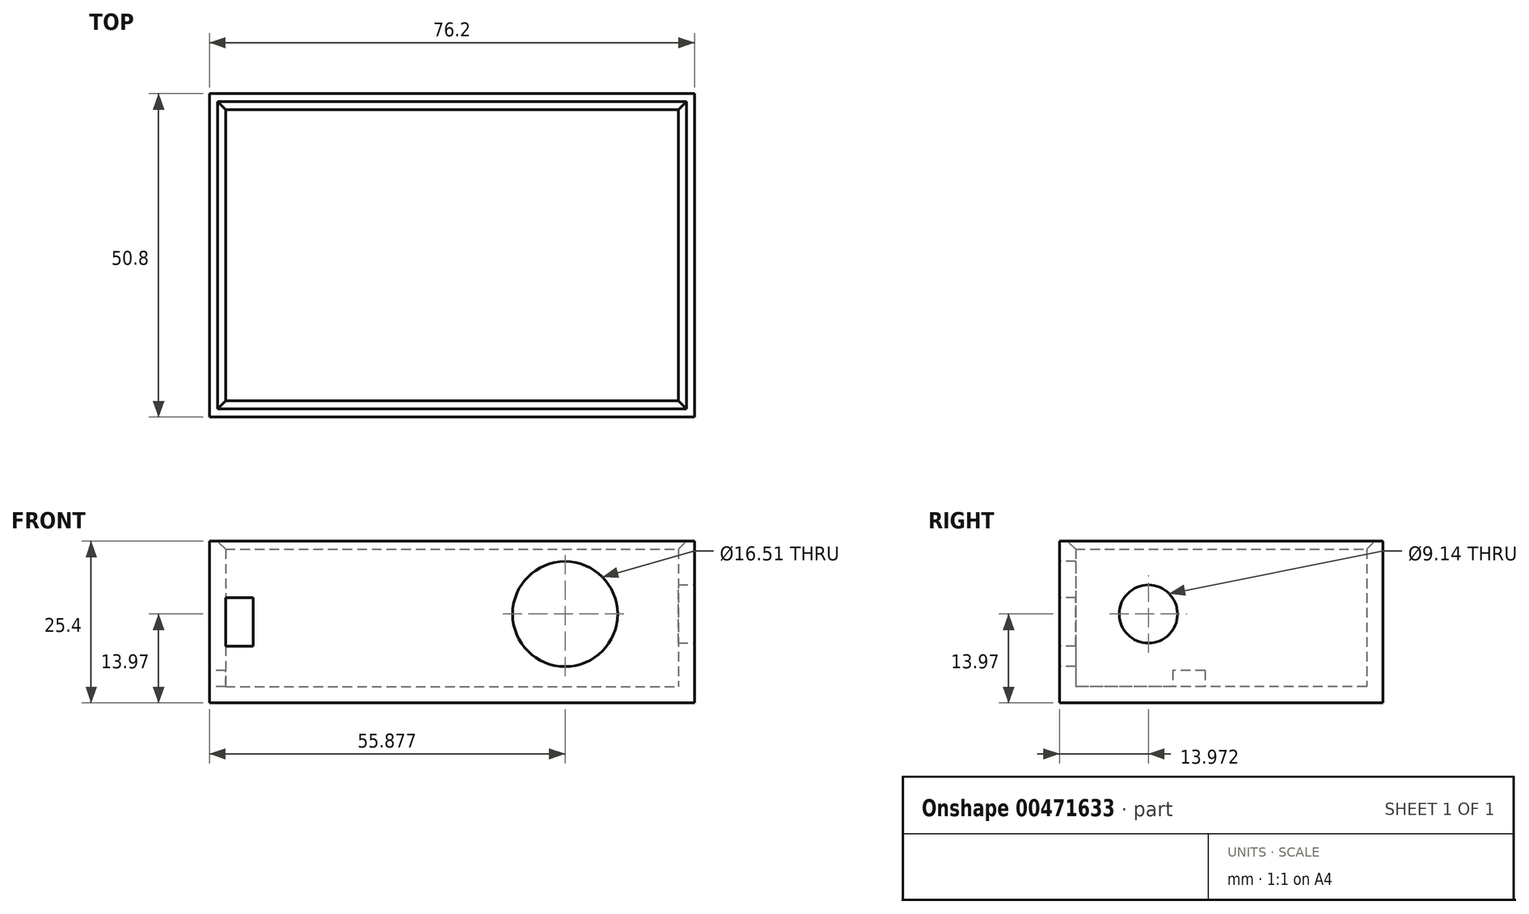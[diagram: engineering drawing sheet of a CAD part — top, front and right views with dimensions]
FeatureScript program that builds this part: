
annotation { "Feature Type Name" : "Feature", "Feature Type Description" : "" }
export const myFeature = defineFeature(function(context is Context, id is Id, definition is map)
    precondition{}
    {
        {
            var Q0;
            Q0=qCreatedBy(makeId("Top.planeOp"),FACE);
            var sketch = newSketch(context, id + "F0", { "sketchPlane" : qUnion([Q0])});
            skLineSegment(sketch, "E0.bottom", {"start": v(-32.94, 25.54) * mm, "end": v(43.26, 25.54) * mm});
            skLineSegment(sketch, "E0.top", {"start": v(-32.94, -25.26) * mm, "end": v(43.26, -25.26) * mm});
            skLineSegment(sketch, "E0.left", {"start": v(-32.94, 25.54) * mm, "end": v(-32.94, -25.26) * mm});
            skLineSegment(sketch, "E0.right", {"start": v(43.26, 25.54) * mm, "end": v(43.26, -25.26) * mm});
            skSolve(sketch);
        }
        {
            var Q0;
            Q0 = qSketchRegion(id + "F0", true);
            extrude(context, id + "F1", {"entities" : qUnion([Q0]), "depth" : 2.54 * mm});
        }
        {
            var Q0;
            Q0=makeQuery(id+"F1.opExtrude","CAP_FACE",FACE,{"disambiguationData":[OSD([sQuery(id+"F0.wireOp",EDGE,"E0.bottom"),sQuery(id+"F0.wireOp",EDGE,"E0.top"),sQuery(id+"F0.wireOp",EDGE,"E0.left"),sQuery(id+"F0.wireOp",EDGE,"E0.right")])],"isStart":false});
            var sketch = newSketch(context, id + "F2", { "sketchPlane" : qUnion([Q0])});
            skLineSegment(sketch, "E1.bottom", {"start": v(-30.4, 23) * mm, "end": v(40.72, 23) * mm});
            skLineSegment(sketch, "E1.top", {"start": v(-30.4, -22.72) * mm, "end": v(40.72, -22.72) * mm});
            skLineSegment(sketch, "E1.left", {"start": v(-30.4, 23) * mm, "end": v(-30.4, -22.72) * mm});
            skLineSegment(sketch, "E1.right", {"start": v(40.72, 23) * mm, "end": v(40.72, -22.72) * mm});
            skLineSegment(sketch, "E2", {"start": v(40.72, -5.9) * mm, "end": v(43.26, -5.9) * mm});
            skLineSegment(sketch, "E3", {"start": v(19.06, -22.72) * mm, "end": v(19.06, -25.26) * mm});
            skSolve(sketch);
        }
        {
            var Q0;
            {var subQ1=sQuery(id+"F2.wireOp",EDGE,"E1.bottom");Q0=makeQuery(id+"F2.imprint","IMPRINT",FACE,{"disambiguationData":[TD([[makeQuery(id+"F2.imprint","IMPRINT",EDGE,{"derivedFrom":subQ1}),1.0]])]});}
            var Q1;
            {var subQ0=sQuery(id+"F2.wireOp",EDGE,"E2");Q1=makeQuery(id+"F2.imprint","IMPRINT",FACE,{"disambiguationData":[TD([[makeQuery(id+"F2.imprint","IMPRINT",EDGE,{"derivedFrom":subQ0}),-1.0]])]});}
            extrude(context, id + "F3", {"entities" : qUnion([Q0, Q1]), "operationType" : NewBodyOperationType.ADD, "depth" : 22.86 * mm});
        }
        {
            var Q0;
            {var subQ0=sQuery(id+"F0.wireOp",EDGE,"E0.top");Q0=makeQuery(id+"F3.boolean.opBoolean","MERGE",FACE,{"derivedFrom":[makeQuery(id+"F1.opExtrude","SWEPT_FACE",FACE,{"disambiguationData":[OSD([subQ0])]}),makeQuery(id+"F3.opExtrude","SWEPT_FACE",FACE,{"disambiguationData":[OSD([subQ0])]})]});}
            var sketch = newSketch(context, id + "F4", { "sketchPlane" : qUnion([Q0])});
            skCircle(sketch, "E4", {"center": v(22.94, 13.97) * mm, "radius": 8.26 * mm});
            skLineSegment(sketch, "E5", {"start": v(22.94, 13.97) * mm, "end": v(43.26, 13.97) * mm});
            skLineSegment(sketch, "E6", {"start": v(22.94, 13.97) * mm, "end": v(22.94, 0) * mm});
            skSolve(sketch);
        }
        {
            var Q0;
            Q0 = qSketchRegion(id + "F4", true);
            extrude(context, id + "F5", {"entities" : qUnion([Q0]), "operationType" : NewBodyOperationType.REMOVE, "oppositeDirection" : true, "depth" : 25.4 * mm});
        }
        {
            var Q0;
            {var subQ0=sQuery(id+"F0.wireOp",EDGE,"E0.right");Q0=makeQuery(id+"F3.boolean.opBoolean","MERGE",FACE,{"derivedFrom":[makeQuery(id+"F1.opExtrude","SWEPT_FACE",FACE,{"disambiguationData":[OSD([subQ0])]}),makeQuery(id+"F3.opExtrude","SWEPT_FACE",FACE,{"disambiguationData":[OSD([subQ0])]})]});}
            var sketch = newSketch(context, id + "F6", { "sketchPlane" : qUnion([Q0])});
            skCircle(sketch, "E7", {"center": v(-11.29, 13.97) * mm, "radius": 4.57 * mm});
            skLineSegment(sketch, "E8", {"start": v(-11.29, 13.97) * mm, "end": v(-11.29, 0) * mm});
            skLineSegment(sketch, "E9", {"start": v(-11.29, 0) * mm, "end": v(-11.29, 13.97) * mm});
            skLineSegment(sketch, "E10", {"start": v(-25.26, 13.97) * mm, "end": v(-11.29, 13.97) * mm});
            skSolve(sketch);
        }
        {
            var Q0;
            Q0 = qSketchRegion(id + "F6", true);
            extrude(context, id + "F7", {"entities" : qUnion([Q0]), "operationType" : NewBodyOperationType.REMOVE, "oppositeDirection" : true, "depth" : 25.4 * mm});
        }
        {
            var Q0;
            {var subQ0=sQuery(id+"F0.wireOp",EDGE,"E0.top");Q0=makeQuery(id+"F3.boolean.opBoolean","MERGE",FACE,{"derivedFrom":[makeQuery(id+"F1.opExtrude","SWEPT_FACE",FACE,{"disambiguationData":[OSD([subQ0])]}),makeQuery(id+"F3.opExtrude","SWEPT_FACE",FACE,{"disambiguationData":[OSD([subQ0])]})]});}
            var sketch = newSketch(context, id + "F8", { "sketchPlane" : qUnion([Q0])});
            skLineSegment(sketch, "E11.bottom", {"start": v(-30.4, 16.51) * mm, "end": v(-26.09, 16.51) * mm});
            skLineSegment(sketch, "E11.top", {"start": v(-30.4, 8.9) * mm, "end": v(-26.09, 8.9) * mm});
            skLineSegment(sketch, "E11.left", {"start": v(-30.4, 16.51) * mm, "end": v(-30.4, 8.9) * mm});
            skLineSegment(sketch, "E11.right", {"start": v(-26.09, 16.51) * mm, "end": v(-26.09, 8.9) * mm});
            skLineSegment(sketch, "E12", {"start": v(-26.09, 8.9) * mm, "end": v(-26.09, 0) * mm});
            skLineSegment(sketch, "E13", {"start": v(-30.4, 8.9) * mm, "end": v(-32.94, 8.9) * mm});
            skSolve(sketch);
        }
        {
            var Q0;
            Q0 = qSketchRegion(id + "F8", true);
            extrude(context, id + "F9", {"entities" : qUnion([Q0]), "operationType" : NewBodyOperationType.REMOVE, "oppositeDirection" : true, "depth" : 25.4 * mm});
        }
        {
            var Q0;
            {var subQ0=sQuery(id+"F0.wireOp",EDGE,"E0.left");Q0=makeQuery(id+"F3.boolean.opBoolean","MERGE",FACE,{"derivedFrom":[makeQuery(id+"F1.opExtrude","SWEPT_FACE",FACE,{"disambiguationData":[OSD([subQ0])]}),makeQuery(id+"F3.opExtrude","SWEPT_FACE",FACE,{"disambiguationData":[OSD([subQ0])]})]});}
            var sketch = newSketch(context, id + "F10", { "sketchPlane" : qUnion([Q0])});
            skLineSegment(sketch, "E14.bottom", {"start": v(2.4, 5.08) * mm, "end": v(7.48, 5.08) * mm});
            skLineSegment(sketch, "E14.top", {"start": v(2.4, 2.54) * mm, "end": v(7.48, 2.54) * mm});
            skLineSegment(sketch, "E14.left", {"start": v(2.4, 5.08) * mm, "end": v(2.4, 2.54) * mm});
            skLineSegment(sketch, "E14.right", {"start": v(7.48, 5.08) * mm, "end": v(7.48, 2.54) * mm});
            skLineSegment(sketch, "E15", {"start": v(7.48, 2.54) * mm, "end": v(7.48, 0) * mm});
            skLineSegment(sketch, "E16", {"start": v(7.48, 2.54) * mm, "end": v(25.26, 2.54) * mm});
            skSolve(sketch);
        }
        {
            var Q0;
            Q0 = qSketchRegion(id + "F10", true);
            extrude(context, id + "F11", {"entities" : qUnion([Q0]), "operationType" : NewBodyOperationType.REMOVE, "oppositeDirection" : true, "depth" : 25.4 * mm});
        }
        {
            var Q0;
            Q0=makeQuery(id+"F3.opExtrude","CAP_EDGE",EDGE,{"disambiguationData":[OSD([sQuery(id+"F2.wireOp",EDGE,"E1.bottom")])],"isStart":false});
            var Q1;
            Q1=makeQuery(id+"F3.opExtrude","CAP_EDGE",EDGE,{"disambiguationData":[OSD([sQuery(id+"F2.wireOp",EDGE,"E1.left")])],"isStart":false});
            var Q2;
            Q2=makeQuery(id+"F3.opExtrude","CAP_EDGE",EDGE,{"disambiguationData":[OSD([sQuery(id+"F2.wireOp",EDGE,"E1.right")])],"isStart":false});
            var Q3;
            Q3=makeQuery(id+"F3.opExtrude","CAP_EDGE",EDGE,{"disambiguationData":[OSD([sQuery(id+"F2.wireOp",EDGE,"E1.top")])],"isStart":false});
            chamfer(context, id + "F12", {"entities" : qUnion([Q0, Q1, Q2, Q3]), "width" : 1.27 * mm, "tangentPropagation" : true});
        }
    });
